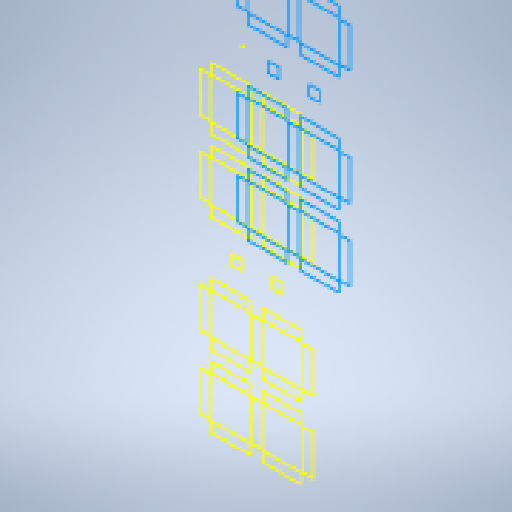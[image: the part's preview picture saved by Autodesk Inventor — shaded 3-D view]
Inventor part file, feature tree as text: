
AUTODESK INVENTOR PART (.ipt)
format: ipt  version: 2024.2 (Build 282272000, 272)  size: 157,696 bytes
history: native  units: mm
features: reference x31, other x7, sketch x1
ambient origin geometry x8: Origin, YZ Plane, XZ Plane, XY Plane, X Axis, Y Axis, Z Axis, Center Point
feature tree (39):
  sketch  "Sketch1"
  reference  "Reference1"
  reference  "Reference2"
  reference  "Reference3"
  reference  "Reference4"
  reference  "Reference5"
  reference  "Reference6"
  reference  "Reference7"
  reference  "Reference8"
  reference  "Reference9"
  reference  "Reference10"
  reference  "Reference11"
  reference  "Reference12"
  reference  "Reference13"
  reference  "Reference14"
  reference  "Reference15"
  reference  "Reference16"
  reference  "Reference17"
  reference  "Reference18"
  reference  "Reference19"
  reference  "Reference20"
  reference  "Reference21"
  reference  "Reference22"
  reference  "Reference23"
  reference  "Reference24"
  reference  "Reference25"
  reference  "Reference26"
  reference  "Reference27"
  reference  "Reference28"
  reference  "Reference29"
  reference  "Reference30"
  reference  "Reference31"
  parser-record x1  (decoder bookkeeping rows leaked as tree rows — omitted from the tree; the rows remain in map.json)
  other  "ClockFace.iam"
  other  "Digit:5"
  other  "Digit:4"
  other  "Dots2:1"
  other  "Digit:3"
  other  "Digit:2"
note: 1 file-system path scrubbed to <path> (originals preserved in map.json)
